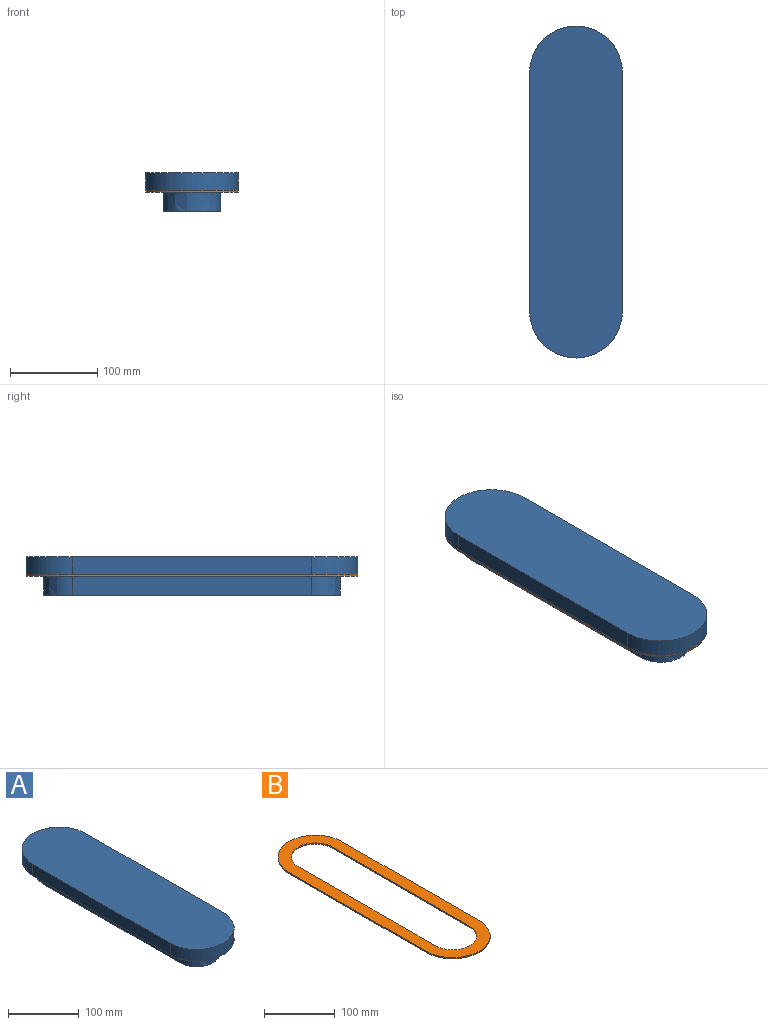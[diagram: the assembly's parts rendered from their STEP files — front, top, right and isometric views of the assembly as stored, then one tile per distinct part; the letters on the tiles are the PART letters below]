
ASSEMBLY  parts=2 mates=1
PART A: 11 faces, bbox 106x380x44 mm
  f0: plane 274x24mm, normal (1,0,0), area 6576mm2, adj f1,f3,f4,f9
  f1: extruded ~66x33mm, area 2488.1mm2, adj f0,f2,f4,f9
  f2: plane 274x24mm, normal (-1,0,0), area 6576mm2, adj f1,f3,f4,f9
  f3: extruded ~66x33mm, area 2488.1mm2, adj f0,f2,f4,f9
  f4: plane 359.8x66mm, normal (0,0,-1), area 21505.8mm2, adj f0,f1,f2,f3
  f5: plane 274x20mm, normal (1,0,0), area 5480mm2, adj f6,f8,f9,f10
  f6: cylinder r=53mm len=106mm, axis (0,0,1), area 3330.1mm2, adj f5,f7,f9,f10
  f7: plane 274x20mm, normal (-1,0,0), area 5480mm2, adj f6,f8,f9,f10
  f8: cylinder r=53mm len=106mm, axis (0,0,1), area 3330.1mm2, adj f5,f7,f9,f10
  f9: plane 380x106mm, normal (0,0,-1), area 16363mm2, adj f0,f1,f2,f3,f5,f6,f7,f8
  f10: plane 380x106mm, normal (0,0,1), area 37868.7mm2, adj f5,f6,f7,f8
PART B: 10 faces, bbox 106x380x2 mm
  f0: plane 274x2mm, normal (1,0,0), area 548mm2, adj f1,f7,f8,f9
  f1: cylinder r=53mm len=106mm, axis (0,0,-1), area 333mm2, adj f0,f2,f8,f9
  f2: plane 274x2mm, normal (-1,0,0), area 548mm2, adj f1,f7,f8,f9
  f3: cylinder r=34mm len=68mm, axis (0,0,-1), area 213.6mm2, adj f4,f6,f8,f9
  f4: plane 274x2mm, normal (-1,0,0), area 548mm2, adj f3,f5,f8,f9
  f5: cylinder r=34mm len=68mm, axis (0,0,-1), area 213.6mm2, adj f4,f6,f8,f9
  f6: plane 274x2mm, normal (1,0,0), area 548mm2, adj f3,f5,f8,f9
  f7: cylinder r=53mm len=106mm, axis (0,0,-1), area 333mm2, adj f0,f2,f8,f9
  f8: plane 380x106mm, normal (0,0,1), area 15605.1mm2, adj f0,f1,f2,f3,f4,f5,f6,f7
  f9: plane 380x106mm, normal (0,0,-1), area 15605.1mm2, adj f0,f1,f2,f3,f4,f5,f6,f7
PLACE A t=(0,0,-34.2)mm
PLACE B t=(0,0,-56.2)mm
MATE fastened A.f9 <-> B.f8  axis (0,0,-1) through (0,0,-54.2)mm
